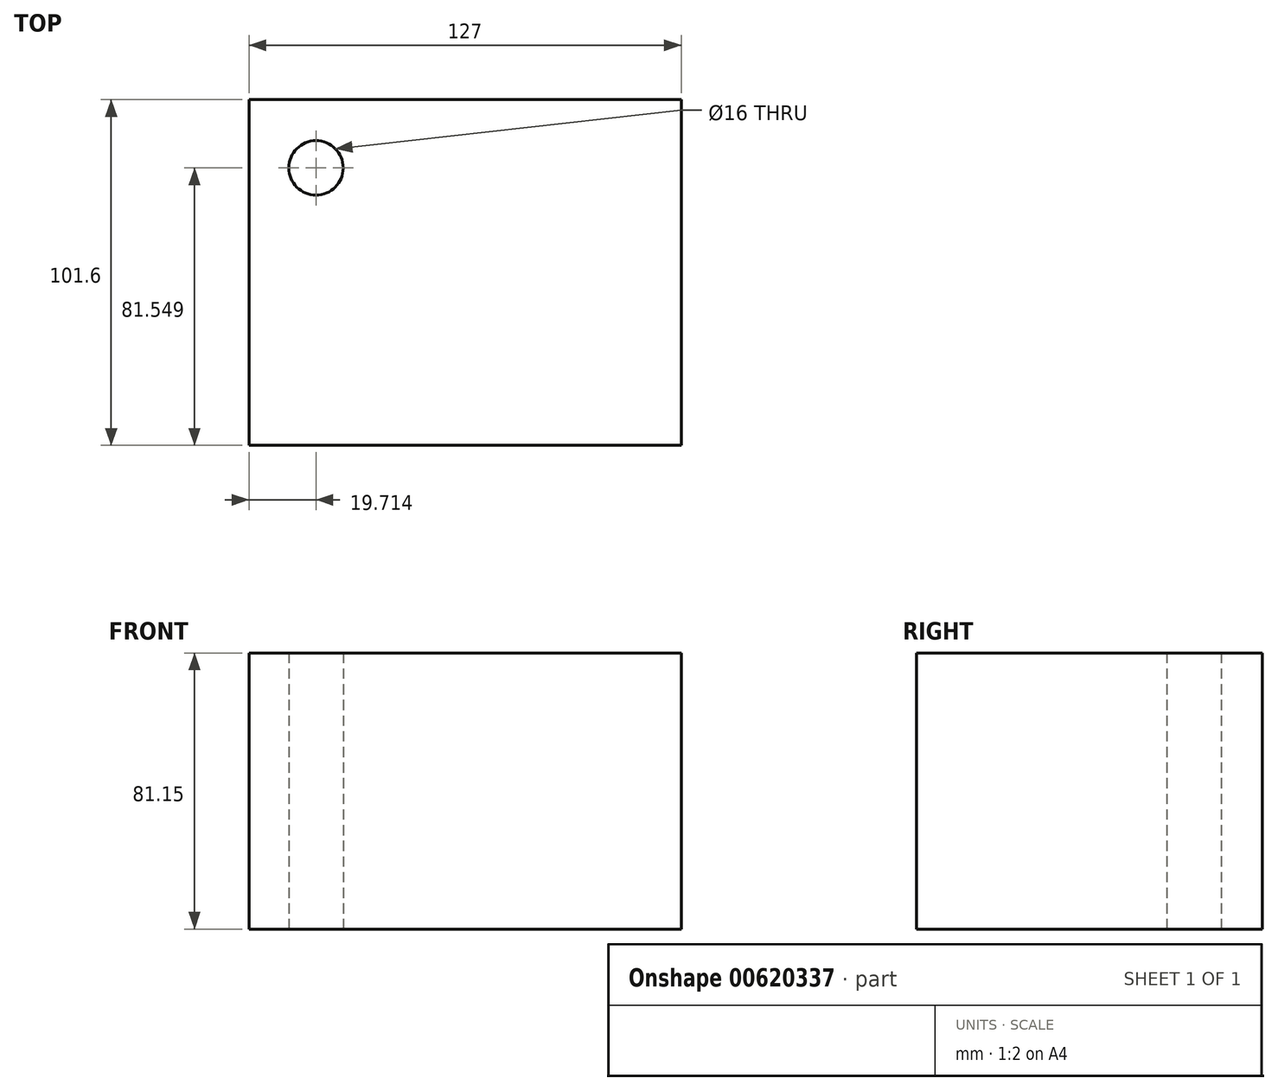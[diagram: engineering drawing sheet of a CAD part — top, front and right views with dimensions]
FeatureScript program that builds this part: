
annotation { "Feature Type Name" : "Feature", "Feature Type Description" : "" }
export const myFeature = defineFeature(function(context is Context, id is Id, definition is map)
    precondition{}
    {
        {
            var Q0;
            Q0=qCreatedBy(makeId("Top.planeOp"),FACE);
            var sketch = newSketch(context, id + "F0", { "sketchPlane" : qUnion([Q0])});
            skLineSegment(sketch, "E0.bottom", {"start": v(63.5, -50.8) * mm, "end": v(-63.5, -50.8) * mm});
            skLineSegment(sketch, "E0.top", {"start": v(63.5, 50.8) * mm, "end": v(-63.5, 50.8) * mm});
            skLineSegment(sketch, "E0.left", {"start": v(63.5, -50.8) * mm, "end": v(63.5, 50.8) * mm});
            skLineSegment(sketch, "E0.right", {"start": v(-63.5, -50.8) * mm, "end": v(-63.5, 50.8) * mm});
            skPoint(sketch, "E0.middle", {"position": v(0, 0) * mm});
            skCircle(sketch, "E1", {"center": v(-43.79, 30.75) * mm, "radius": 8 * mm});
            skSolve(sketch);
        }
        {
            var Q0;
            Q0=makeQuery(id+"F0.imprint","IMPRINT",FACE,{"disambiguationData":[TD([[makeQuery(id+"F0.imprint","IMPRINT",EDGE,{"derivedFrom":sQuery(id+"F0.wireOp",EDGE,"E0.bottom")}),-1.0]])]});
            extrude(context, id + "F1", {"entities" : qUnion([Q0]), "depth" : 81.15 * mm, "offsetDistance" : 25.4 * mm});
        }
    });
